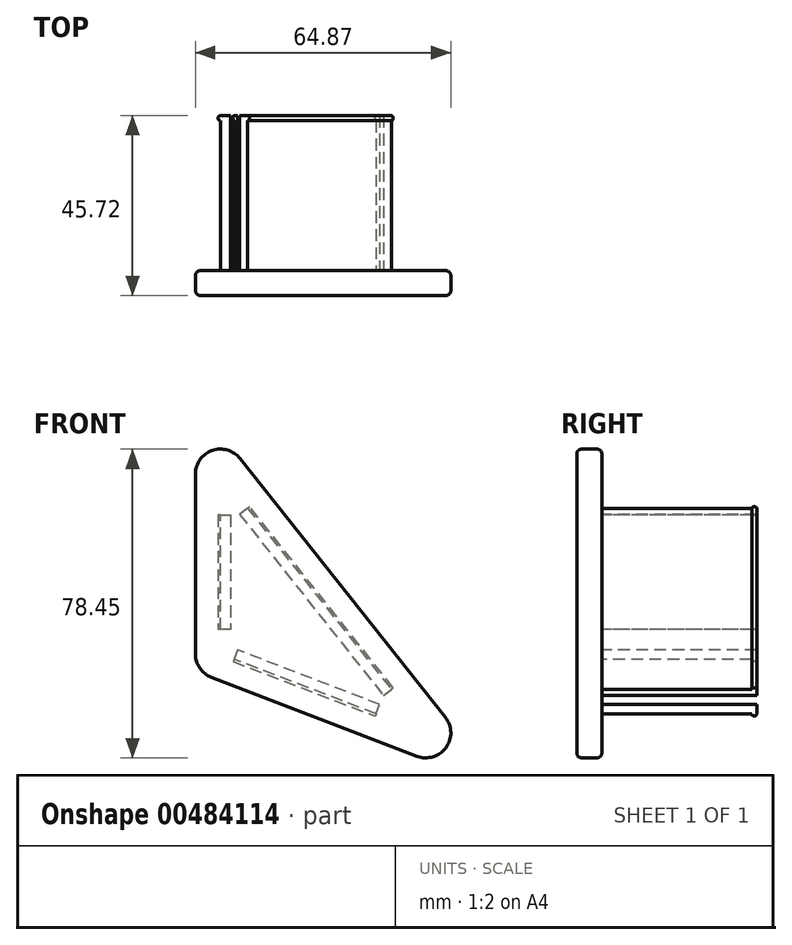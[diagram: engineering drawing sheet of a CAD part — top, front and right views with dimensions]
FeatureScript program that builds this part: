
annotation { "Feature Type Name" : "Feature", "Feature Type Description" : "" }
export const myFeature = defineFeature(function(context is Context, id is Id, definition is map)
    precondition{}
    {
        {
            var Q0;
            Q0=qCreatedBy(makeId("Front.planeOp"),FACE);
            var sketch = newSketch(context, id + "F0", { "sketchPlane" : qUnion([Q0])});
            skLineSegment(sketch, "E0", {"start": v(0, 0) * mm, "end": v(0, -45.72) * mm});
            skLineSegment(sketch, "E1", {"start": v(0, -45.72) * mm, "end": v(52.17, -65.75) * mm});
            skLineSegment(sketch, "E2", {"start": v(0, 0) * mm, "end": v(52.17, -65.75) * mm});
            skLineSegment(sketch, "E3.0", {"start": v(4.97, 3.95) * mm, "end": v(57.14, -61.8) * mm});
            skLineSegment(sketch, "E3.1", {"start": v(-6.35, 0) * mm, "end": v(-6.35, -45.72) * mm});
            skLineSegment(sketch, "E3.2", {"start": v(-2.28, -51.65) * mm, "end": v(49.9, -71.67) * mm});
            skLineSegment(sketch, "E4", {"start": v(0, -10.38) * mm, "end": v(2.54, -10.38) * mm});
            skLineSegment(sketch, "E5", {"start": v(2.54, -10.38) * mm, "end": v(2.54, -39.52) * mm});
            skLineSegment(sketch, "E6", {"start": v(2.54, -39.52) * mm, "end": v(0, -39.52) * mm});
            skLineSegment(sketch, "E7", {"start": v(6.88, -8.67) * mm, "end": v(4.9, -10.25) * mm});
            skLineSegment(sketch, "E8", {"start": v(4.9, -10.25) * mm, "end": v(41.4, -56.27) * mm});
            skLineSegment(sketch, "E9", {"start": v(41.4, -56.27) * mm, "end": v(43.4, -54.69) * mm});
            skLineSegment(sketch, "E10", {"start": v(39.54, -60.9) * mm, "end": v(40.45, -58.53) * mm});
            skLineSegment(sketch, "E11", {"start": v(40.45, -58.53) * mm, "end": v(4.37, -44.68) * mm});
            skLineSegment(sketch, "E12", {"start": v(4.37, -44.68) * mm, "end": v(3.46, -47.05) * mm});
            skPoint(sketch, "E13.visualSharp", {"position": v(71.59, -80) * mm});
            skArc(sketch, "E13.filletArc", {"start": v(49.9, -71.67) * mm, "mid": v(57.29, -69.5) * mm, "end": v(57.14, -61.8) * mm});
            skPoint(sketch, "E14.visualSharp", {"position": v(-6.35, -50.08) * mm});
            skArc(sketch, "E14.filletArc", {"start": v(-6.35, -45.72) * mm, "mid": v(-5.23, -49.32) * mm, "end": v(-2.28, -51.65) * mm});
            skPoint(sketch, "E15.visualSharp", {"position": v(-6.35, 18.22) * mm});
            skArc(sketch, "E15.filletArc", {"start": v(4.97, 3.95) * mm, "mid": v(-2.09, 6) * mm, "end": v(-6.35, 0) * mm});
            skSolve(sketch);
        }
        {
            var Q0;
            Q0=makeQuery(id+"F0.imprint","IMPRINT",FACE,{"disambiguationData":[TD([[makeQuery(id+"F0.imprint","IMPRINT",EDGE,{"derivedFrom":sQuery(id+"F0.wireOp",EDGE,"E0")}),-1.0]])]});
            var Q1;
            Q1=makeQuery(id+"F0.imprint","IMPRINT",FACE,{"disambiguationData":[TD([[makeQuery(id+"F0.imprint","IMPRINT",EDGE,{"derivedFrom":sQuery(id+"F0.wireOp",EDGE,"E0")}),1.0]])]});
            var Q2;
            {var subQ0=sQuery(id+"F0.wireOp",EDGE,"E4");Q2=makeQuery(id+"F0.imprint","IMPRINT",FACE,{"disambiguationData":[TD([[makeQuery(id+"F0.imprint","IMPRINT",EDGE,{"derivedFrom":subQ0}),-1.0]])]});}
            var Q3;
            {var subQ0=sQuery(id+"F0.wireOp",EDGE,"E7");Q3=makeQuery(id+"F0.imprint","IMPRINT",FACE,{"disambiguationData":[TD([[makeQuery(id+"F0.imprint","IMPRINT",EDGE,{"derivedFrom":subQ0}),1.0]])]});}
            var Q4;
            {var subQ0=sQuery(id+"F0.wireOp",EDGE,"E10");Q4=makeQuery(id+"F0.imprint","IMPRINT",FACE,{"disambiguationData":[TD([[makeQuery(id+"F0.imprint","IMPRINT",EDGE,{"derivedFrom":subQ0}),1.0]])]});}
            extrude(context, id + "F1", {"entities" : qUnion([Q0, Q1, Q2, Q3, Q4]), "depth" : 6.35 * mm, "offsetDistance" : 25.4 * mm});
        }
        {
            var Q0;
            {var subQ0=sQuery(id+"F0.wireOp",EDGE,"E4");Q0=makeQuery(id+"F0.imprint","IMPRINT",FACE,{"disambiguationData":[TD([[makeQuery(id+"F0.imprint","IMPRINT",EDGE,{"derivedFrom":subQ0}),-1.0]])]});}
            var Q1;
            {var subQ0=sQuery(id+"F0.wireOp",EDGE,"E10");Q1=makeQuery(id+"F0.imprint","IMPRINT",FACE,{"disambiguationData":[TD([[makeQuery(id+"F0.imprint","IMPRINT",EDGE,{"derivedFrom":subQ0}),1.0]])]});}
            var Q2;
            {var subQ0=sQuery(id+"F0.wireOp",EDGE,"E7");Q2=makeQuery(id+"F0.imprint","IMPRINT",FACE,{"disambiguationData":[TD([[makeQuery(id+"F0.imprint","IMPRINT",EDGE,{"derivedFrom":subQ0}),1.0]])]});}
            extrude(context, id + "F2", {"entities" : qUnion([Q0, Q1, Q2]), "oppositeDirection" : true, "depth" : 39.37 * mm, "offsetDistance" : 25.4 * mm});
        }
        {
            var Q0;
            Q0=makeQuery(id+"F2.opExtrude","SWEPT_FACE",FACE,{"disambiguationData":[OSD([sQuery(id+"F0.wireOp",EDGE,"E2")])]});
            var sketch = newSketch(context, id + "F3", { "sketchPlane" : qUnion([Q0])});
            skLineSegment(sketch, "E16", {"start": v(38.1, -11.07) * mm, "end": v(38.1, -69.81) * mm});
            skSolve(sketch);
        }
        {
            var Q0;
            {var subQ0=sQuery(id+"F3.wireOp",EDGE,"E16");Q0=makeQuery(id+"F3.imprint","IMPRINT",FACE,{"disambiguationData":[TD([[makeQuery(id+"F3.imprint","IMPRINT",EDGE,{"derivedFrom":subQ0}),1.0]])]});}
            extrude(context, id + "F4", {"entities" : qUnion([Q0]), "operationType" : NewBodyOperationType.ADD, "depth" : 0.64 * mm, "offsetDistance" : 25.4 * mm});
        }
        {
            var Q0;
            Q0=makeQuery(id+"F4.opExtrude","CAP_EDGE",EDGE,{"disambiguationData":[OSD([sQuery(id+"F3.wireOp",EDGE,"E16")])],"isStart":false});
            var Q1;
            Q1=makeQuery(id+"F4.opExtrude","CAP_EDGE",EDGE,{"disambiguationData":[OSD([sQuery(id+"F0.wireOp",EDGE,"E2")])],"isStart":false});
            fillet(context, id + "F5", {"entities" : qUnion([Q0, Q1]), "radius" : 0.64 * mm, "tangentPropagation" : true, "allowEdgeOverflow" : false});
        }
        {
            var Q0;
            Q0=makeQuery(id+"F2.opExtrude","SWEPT_FACE",FACE,{"disambiguationData":[OSD([sQuery(id+"F0.wireOp",EDGE,"E1")])]});
            var sketch = newSketch(context, id + "F6", { "sketchPlane" : qUnion([Q0])});
            skLineSegment(sketch, "E17", {"start": v(58.74, -38.1) * mm, "end": v(20.09, -38.1) * mm});
            skSolve(sketch);
        }
        {
            var Q0;
            {var subQ0=sQuery(id+"F6.wireOp",EDGE,"E17");Q0=makeQuery(id+"F6.imprint","IMPRINT",FACE,{"disambiguationData":[TD([[makeQuery(id+"F6.imprint","IMPRINT",EDGE,{"derivedFrom":subQ0}),1.0]])]});}
            extrude(context, id + "F7", {"entities" : qUnion([Q0]), "operationType" : NewBodyOperationType.ADD, "depth" : 0.64 * mm, "offsetDistance" : 25.4 * mm});
        }
        {
            var Q0;
            Q0=makeQuery(id+"F7.opExtrude","CAP_EDGE",EDGE,{"disambiguationData":[OSD([sQuery(id+"F6.wireOp",EDGE,"E17")])],"isStart":false});
            var Q1;
            Q1=makeQuery(id+"F7.opExtrude","CAP_EDGE",EDGE,{"disambiguationData":[OSD([sQuery(id+"F0.wireOp",EDGE,"E1")])],"isStart":false});
            fillet(context, id + "F8", {"entities" : qUnion([Q0, Q1]), "radius" : 0.64 * mm, "tangentPropagation" : true, "allowEdgeOverflow" : false});
        }
        {
            var Q0;
            Q0=makeQuery(id+"F2.opExtrude","SWEPT_FACE",FACE,{"disambiguationData":[OSD([sQuery(id+"F0.wireOp",EDGE,"E0")])]});
            var sketch = newSketch(context, id + "F9", { "sketchPlane" : qUnion([Q0])});
            skLineSegment(sketch, "E18", {"start": v(-38.1, -39.52) * mm, "end": v(-38.1, -10.38) * mm});
            skSolve(sketch);
        }
        {
            var Q0;
            {var subQ0=sQuery(id+"F9.wireOp",EDGE,"E18");Q0=makeQuery(id+"F9.imprint","IMPRINT",FACE,{"disambiguationData":[TD([[makeQuery(id+"F9.imprint","IMPRINT",EDGE,{"derivedFrom":subQ0}),1.0]])]});}
            extrude(context, id + "F10", {"entities" : qUnion([Q0]), "operationType" : NewBodyOperationType.ADD, "depth" : 0.64 * mm, "offsetDistance" : 25.4 * mm});
        }
        {
            var Q0;
            Q0=makeQuery(id+"F10.opExtrude","CAP_EDGE",EDGE,{"disambiguationData":[OSD([sQuery(id+"F9.wireOp",EDGE,"E18")])],"isStart":false});
            var Q1;
            Q1=makeQuery(id+"F10.opExtrude","CAP_EDGE",EDGE,{"disambiguationData":[OSD([sQuery(id+"F0.wireOp",EDGE,"E0")])],"isStart":false});
            fillet(context, id + "F11", {"entities" : qUnion([Q0, Q1]), "radius" : 0.64 * mm, "tangentPropagation" : true, "allowEdgeOverflow" : false});
        }
        {
            var Q0;
            Q0=makeQuery(id+"F1.opExtrude","CAP_EDGE",EDGE,{"disambiguationData":[OSD([sQuery(id+"F0.wireOp",EDGE,"E3.1")])],"isStart":false});
            var Q1;
            Q1=makeQuery(id+"F1.opExtrude","CAP_EDGE",EDGE,{"disambiguationData":[OSD([sQuery(id+"F0.wireOp",EDGE,"E3.1")])],"isStart":true});
            fillet(context, id + "F12", {"entities" : qUnion([Q0, Q1]), "radius" : 1.27 * mm, "tangentPropagation" : true, "allowEdgeOverflow" : false});
        }
    });
